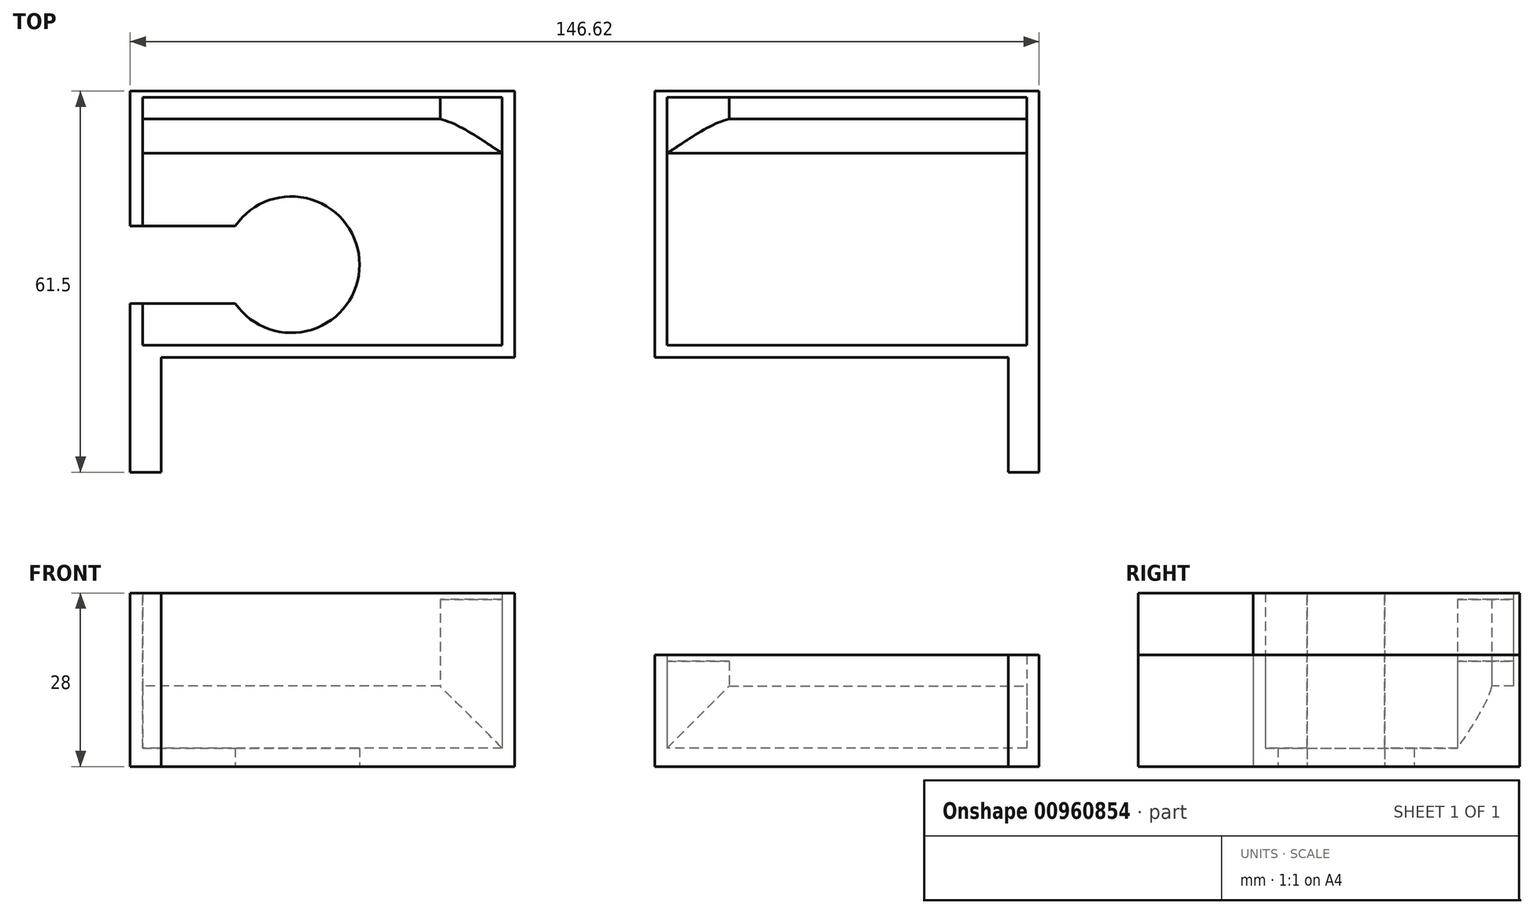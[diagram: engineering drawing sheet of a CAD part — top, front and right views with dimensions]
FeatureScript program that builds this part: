
annotation { "Feature Type Name" : "Feature", "Feature Type Description" : "" }
export const myFeature = defineFeature(function(context is Context, id is Id, definition is map)
    precondition{}
    {
        {
            var Q0;
            Q0=qCreatedBy(makeId("Top.planeOp"),FACE);
            var sketch = newSketch(context, id + "F0", { "sketchPlane" : qUnion([Q0])});
            skLineSegment(sketch, "E0.bottom", {"start": v(11.31, 34.26) * mm, "end": v(73.31, 34.26) * mm});
            skLineSegment(sketch, "E0.left", {"start": v(11.31, 34.26) * mm, "end": v(11.31, -8.74) * mm});
            skLineSegment(sketch, "E0.right", {"start": v(73.31, 34.26) * mm, "end": v(73.31, -8.74) * mm});
            skLineSegment(sketch, "E1", {"start": v(11.31, -8.74) * mm, "end": v(73.31, -8.74) * mm});
            skLineSegment(sketch, "E2.bottom", {"start": v(73.31, -8.74) * mm, "end": v(68.31, -8.74) * mm});
            skLineSegment(sketch, "E2.top", {"start": v(73.31, -27.24) * mm, "end": v(68.31, -27.24) * mm});
            skLineSegment(sketch, "E2.left", {"start": v(73.31, -8.74) * mm, "end": v(73.31, -27.24) * mm});
            skLineSegment(sketch, "E2.right", {"start": v(68.31, -8.74) * mm, "end": v(68.31, -27.24) * mm});
            skFitSpline(sketch, "E3", {"points": [v(68.31, -27.24) * mm, v(19.3, -23.74) * mm, v(11.31, -26.1) * mm], "startDerivative": vector(-136.82, 11.05) * mm, "endDerivative": vector(-34.36, -17.66) * mm});
            skFitSpline(sketch, "E4.0", {"points": [v(68.07, -30.23) * mm, v(56.66, -29.31) * mm, v(43.66, -28.17) * mm, v(32.2, -27.2) * mm, v(27.01, -26.83) * mm, v(23.77, -26.68) * mm, v(21.72, -26.65) * mm, v(20.28, -26.69) * mm, v(19.24, -26.75) * mm, v(18.29, -26.84) * mm, v(17.23, -27) * mm, v(15.98, -27.33) * mm, v(14.53, -27.87) * mm, v(13.35, -28.44) * mm, v(12.68, -28.78) * mm]});
            skLineSegment(sketch, "E5", {"start": v(73.31, -30.15) * mm, "end": v(73.31, -27.24) * mm});
            skLineSegment(sketch, "E6", {"start": v(13.28, -28.48) * mm, "end": v(11.31, -26.1) * mm});
            skLineSegment(sketch, "E7", {"start": v(66.53, -30.1) * mm, "end": v(73.31, -30.15) * mm});
            skSolve(sketch);
        }
        {
            var Q0;
            Q0 = qSketchRegion(id + "F0", true);
            extrude(context, id + "F1", {"entities" : qUnion([Q0]), "depth" : 3 * mm, "offsetDistance" : 25 * mm});
        }
        {
            var Q0;
            Q0=makeQuery(id+"F1.opExtrude","CAP_FACE",FACE,{"disambiguationData":[OSD([sQuery(id+"F0.wireOp",EDGE,"E0.bottom"),sQuery(id+"F0.wireOp",EDGE,"E0.left"),sQuery(id+"F0.wireOp",EDGE,"E0.right"),sQuery(id+"F0.wireOp",EDGE,"E1"),sQuery(id+"F0.wireOp",EDGE,"E2.left"),sQuery(id+"F0.wireOp",EDGE,"E2.right"),sQuery(id+"F0.wireOp",EDGE,"E3"),sQuery(id+"F0.wireOp",EDGE,"E4.0"),sQuery(id+"F0.wireOp",EDGE,"E5"),sQuery(id+"F0.wireOp",EDGE,"E6"),sQuery(id+"F0.wireOp",EDGE,"E7")])],"isStart":false});
            var sketch = newSketch(context, id + "F2", { "sketchPlane" : qUnion([Q0])});
            skLineSegment(sketch, "E8", {"start": v(11.31, 34.26) * mm, "end": v(11.31, -8.74) * mm});
            skLineSegment(sketch, "E9", {"start": v(11.31, -8.74) * mm, "end": v(73.31, -8.74) * mm});
            skLineSegment(sketch, "E10", {"start": v(73.31, -8.74) * mm, "end": v(73.31, 34.26) * mm});
            skLineSegment(sketch, "E11", {"start": v(73.31, 34.26) * mm, "end": v(11.31, 34.26) * mm});
            skLineSegment(sketch, "E12", {"start": v(13.31, -6.74) * mm, "end": v(13.31, 33.26) * mm});
            skLineSegment(sketch, "E13", {"start": v(13.31, 33.26) * mm, "end": v(71.31, 33.26) * mm});
            skLineSegment(sketch, "E14", {"start": v(71.31, 33.26) * mm, "end": v(71.31, -6.74) * mm});
            skLineSegment(sketch, "E15", {"start": v(71.31, -6.74) * mm, "end": v(13.31, -6.74) * mm});
            skSolve(sketch);
        }
        {
            var Q0;
            {var subQ3=sQuery(id+"F2.wireOp",EDGE,"E8");Q0=makeQuery(id+"F2.imprint","IMPRINT",FACE,{"disambiguationData":[TD([[makeQuery(id+"F2.imprint","IMPRINT",EDGE,{"derivedFrom":subQ3}),1.0]])]});}
            var Q1;
            {var subQ0=makeQuery(id+"F1.opExtrude","CAP_EDGE",EDGE,{"disambiguationData":[OSD([sQuery(id+"F0.wireOp",EDGE,"E2.right")])],"isStart":false});Q1=makeQuery(id+"F2.imprint","IMPRINT",FACE,{"disambiguationData":[TD([[makeQuery(id+"F2.imprint","IMPRINT",EDGE,{"derivedFrom":subQ0}),1.0]])]});}
            extrude(context, id + "F3", {"entities" : qUnion([Q0, Q1]), "operationType" : NewBodyOperationType.ADD, "depth" : 15 * mm, "offsetDistance" : 25 * mm});
        }
        {
            var Q0;
            Q0=makeQuery(id+"F3.opExtrude","SWEPT_FACE",FACE,{"disambiguationData":[OSD([sQuery(id+"F2.wireOp",EDGE,"E14")])]});
            var sketch = newSketch(context, id + "F4", { "sketchPlane" : qUnion([Q0])});
            skLineSegment(sketch, "E16", {"start": v(-33.26, 3) * mm, "end": v(-33.26, 13) * mm});
            skLineSegment(sketch, "E17", {"start": v(-33.26, 13) * mm, "end": v(-29.76, 13) * mm});
            skLineSegment(sketch, "E18", {"start": v(-24.26, 3) * mm, "end": v(-33.26, 3) * mm});
            skFitSpline(sketch, "E19", {"points": [v(-29.76, 13) * mm, v(-24.26, 3) * mm], "startDerivative": vector(2.23, -9.8) * mm, "endDerivative": vector(4.97, -8) * mm});
            skSolve(sketch);
        }
        {
            var Q0;
            Q0=makeQuery(id+"F4.imprint","IMPRINT",FACE,{"disambiguationData":[TD([[makeQuery(id+"F4.imprint","IMPRINT",EDGE,{"derivedFrom":sQuery(id+"F4.wireOp",EDGE,"E16")}),1.0]])]});
            extrude(context, id + "F5", {"entities" : qUnion([Q0]), "operationType" : NewBodyOperationType.ADD, "endBound" : BoundingType.UP_TO_NEXT, "depth" : 25 * mm, "offsetDistance" : 25 * mm});
        }
        {
            var Q0;
            Q0=makeQuery(id+"F1.opExtrude","CAP_FACE",FACE,{"disambiguationData":[OSD([sQuery(id+"F0.wireOp",EDGE,"E0.bottom"),sQuery(id+"F0.wireOp",EDGE,"E0.left"),sQuery(id+"F0.wireOp",EDGE,"E0.right"),sQuery(id+"F0.wireOp",EDGE,"E1"),sQuery(id+"F0.wireOp",EDGE,"E2.left"),sQuery(id+"F0.wireOp",EDGE,"E2.right"),sQuery(id+"F0.wireOp",EDGE,"E3"),sQuery(id+"F0.wireOp",EDGE,"E4.0"),sQuery(id+"F0.wireOp",EDGE,"E5"),sQuery(id+"F0.wireOp",EDGE,"E6"),sQuery(id+"F0.wireOp",EDGE,"E7")])],"isStart":false});
            var sketch = newSketch(context, id + "F6", { "sketchPlane" : qUnion([Q0])});
            skLineSegment(sketch, "E20", {"start": v(13.31, 33.26) * mm, "end": v(23.31, 33.26) * mm});
            skLineSegment(sketch, "E21", {"start": v(23.31, 33.26) * mm, "end": v(23.31, 29.76) * mm});
            skLineSegment(sketch, "E22", {"start": v(13.31, 24.26) * mm, "end": v(13.31, 33.26) * mm});
            skFitSpline(sketch, "E23", {"points": [v(23.31, 29.76) * mm, v(13.31, 24.26) * mm], "startDerivative": vector(-9.8, -2.23) * mm, "endDerivative": vector(-8, -4.97) * mm});
            skLineSegment(sketch, "E24.0", {"start": v(13.31, -6.74) * mm, "end": v(13.31, 24.26) * mm});
            skLineSegment(sketch, "E24.1", {"start": v(13.31, 33.26) * mm, "end": v(71.31, 33.26) * mm});
            skSolve(sketch);
        }
        {
            var Q0;
            Q0=makeQuery(id+"F6.imprint","IMPRINT",FACE,{"disambiguationData":[TD([[makeQuery(id+"F6.imprint","IMPRINT",EDGE,{"derivedFrom":sQuery(id+"F6.wireOp",EDGE,"E20")}),-1.0]])]});
            extrude(context, id + "F7", {"entities" : qUnion([Q0]), "operationType" : NewBodyOperationType.ADD, "depth" : 14 * mm, "offsetDistance" : 25 * mm});
        }
        {
            var Q0;
            Q0=makeQuery(id+"F1.opExtrude","SWEPT_BODY",BODY,{"disambiguationData":[OSD([sQuery(id+"F0.wireOp",EDGE,"E0.bottom"),sQuery(id+"F0.wireOp",EDGE,"E0.left"),sQuery(id+"F0.wireOp",EDGE,"E0.right"),sQuery(id+"F0.wireOp",EDGE,"E1"),sQuery(id+"F0.wireOp",EDGE,"E2.left"),sQuery(id+"F0.wireOp",EDGE,"E2.right"),sQuery(id+"F0.wireOp",EDGE,"E3"),sQuery(id+"F0.wireOp",EDGE,"E4.0"),sQuery(id+"F0.wireOp",EDGE,"E5"),sQuery(id+"F0.wireOp",EDGE,"E6"),sQuery(id+"F0.wireOp",EDGE,"E7")])]});
            var Q1;
            Q1=qCreatedBy(makeId("Right.planeOp"),FACE);
            mirror(context, id + "F8", {"entities" : qUnion([Q0]), "mirrorPlane" : qUnion([Q1])});
        }
        {
            var Q0;
            {Q0=qUnion([makeQuery(id+"F8.opPattern","COPY",FACE,{"derivedFrom":makeQuery(id+"F3.opExtrude","CAP_FACE",FACE,{"disambiguationData":[OSD([sQuery(id+"F0.wireOp",EDGE,"E0.right"),sQuery(id+"F0.wireOp",EDGE,"E2.left"),sQuery(id+"F0.wireOp",EDGE,"E2.right"),sQuery(id+"F0.wireOp",EDGE,"E3"),sQuery(id+"F0.wireOp",EDGE,"E4.0"),sQuery(id+"F0.wireOp",EDGE,"E5"),sQuery(id+"F0.wireOp",EDGE,"E6"),sQuery(id+"F0.wireOp",EDGE,"E7"),sQuery(id+"F2.wireOp",EDGE,"E8"),sQuery(id+"F2.wireOp",EDGE,"E9"),sQuery(id+"F2.wireOp",EDGE,"E10"),sQuery(id+"F2.wireOp",EDGE,"E11"),sQuery(id+"F2.wireOp",EDGE,"E12"),sQuery(id+"F2.wireOp",EDGE,"E13"),sQuery(id+"F2.wireOp",EDGE,"E14"),sQuery(id+"F2.wireOp",EDGE,"E15")])],"isStart":false}),"instanceName":"1"}),makeQuery(id+"F8.opPattern","COPY",FACE,{"derivedFrom":makeQuery(id+"F7.opExtrude","CAP_FACE",FACE,{"disambiguationData":[OSD([sQuery(id+"F6.wireOp",EDGE,"E20"),sQuery(id+"F6.wireOp",EDGE,"E21"),sQuery(id+"F6.wireOp",EDGE,"E22"),sQuery(id+"F6.wireOp",EDGE,"E23")])],"isStart":false}),"instanceName":"1"})]);}
            extrude(context, id + "F9", {"entities" : qUnion([Q0]), "operationType" : NewBodyOperationType.ADD, "depth" : 10 * mm, "offsetDistance" : 25 * mm});
        }
        {
            var Q0;
            Q0=makeQuery(id+"F8.opPattern","COPY",FACE,{"derivedFrom":makeQuery(id+"F1.opExtrude","CAP_FACE",FACE,{"disambiguationData":[OSD([sQuery(id+"F0.wireOp",EDGE,"E0.bottom"),sQuery(id+"F0.wireOp",EDGE,"E0.left"),sQuery(id+"F0.wireOp",EDGE,"E0.right"),sQuery(id+"F0.wireOp",EDGE,"E1"),sQuery(id+"F0.wireOp",EDGE,"E2.left"),sQuery(id+"F0.wireOp",EDGE,"E2.right"),sQuery(id+"F0.wireOp",EDGE,"E3"),sQuery(id+"F0.wireOp",EDGE,"E4.0"),sQuery(id+"F0.wireOp",EDGE,"E5"),sQuery(id+"F0.wireOp",EDGE,"E6"),sQuery(id+"F0.wireOp",EDGE,"E7")])],"isStart":true}),"instanceName":"1"});
            var sketch = newSketch(context, id + "F10", { "sketchPlane" : qUnion([Q0])});
            skCircle(sketch, "E25", {"center": v(-47.31, -6.26) * mm, "radius": 11 * mm});
            skLineSegment(sketch, "E26", {"start": v(-56.36, 0) * mm, "end": v(-73.31, 0) * mm});
            skLineSegment(sketch, "E27", {"start": v(-56.36, -12.5) * mm, "end": v(-73.31, -12.5) * mm});
            skLineSegment(sketch, "E28.0", {"start": v(-73.31, -34.26) * mm, "end": v(-73.31, 30.15) * mm});
            skLineSegment(sketch, "E29", {"start": v(-47.31, -6.26) * mm, "end": v(-73.31, -6.26) * mm, "construction": true});
            skSolve(sketch);
        }
        {
            var Q0;
            Q0 = qSketchRegion(id + "F10", true);
            extrude(context, id + "F11", {"entities" : qUnion([Q0]), "operationType" : NewBodyOperationType.REMOVE, "oppositeDirection" : true, "depth" : 28 * mm, "offsetDistance" : 25 * mm});
        }
    });
